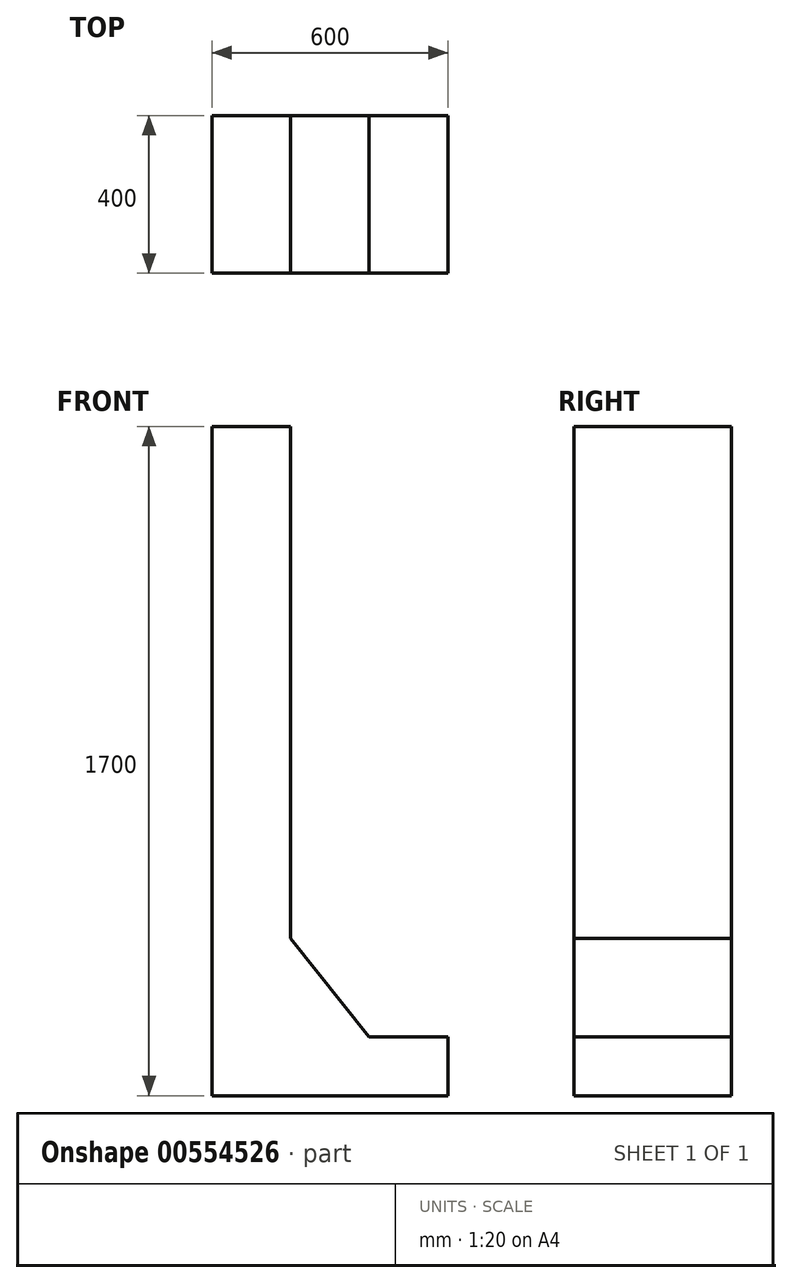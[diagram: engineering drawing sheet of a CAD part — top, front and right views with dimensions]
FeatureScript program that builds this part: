
annotation { "Feature Type Name" : "Feature", "Feature Type Description" : "" }
export const myFeature = defineFeature(function(context is Context, id is Id, definition is map)
    precondition{}
    {
        {
            var Q0;
            Q0=qCreatedBy(makeId("Front.planeOp"),FACE);
            var sketch = newSketch(context, id + "F0", { "sketchPlane" : qUnion([Q0])});
            skLineSegment(sketch, "E0", {"start": v(-31.75, 0) * mm, "end": v(568.25, 0) * mm});
            skLineSegment(sketch, "E1", {"start": v(-31.75, 0) * mm, "end": v(-31.75, 1700) * mm});
            skLineSegment(sketch, "E2", {"start": v(-31.75, 1700) * mm, "end": v(168.25, 1700) * mm});
            skLineSegment(sketch, "E3", {"start": v(568.25, 0) * mm, "end": v(568.25, 150) * mm});
            skLineSegment(sketch, "E4", {"start": v(568.25, 150) * mm, "end": v(367.43, 150) * mm});
            skLineSegment(sketch, "E5", {"start": v(168.25, 1700) * mm, "end": v(168.25, 400) * mm});
            skLineSegment(sketch, "E6", {"start": v(168.25, 400) * mm, "end": v(367.43, 150) * mm});
            skSolve(sketch);
        }
        {
            var Q0;
            Q0 = qSketchRegion(id + "F0", true);
            extrude(context, id + "F1", {"entities" : qUnion([Q0]), "depth" : 400 * mm, "offsetDistance" : 25 * mm});
        }
    });
